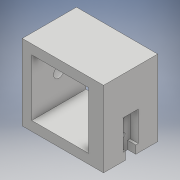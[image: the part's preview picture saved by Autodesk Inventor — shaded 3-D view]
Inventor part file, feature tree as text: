
AUTODESK INVENTOR PART (.ipt)
format: ipt  version: 2017 (Build 210142000, 142)  size: 137,728 bytes
history: native  units: mm
features: extrude x4, sketch x3
ambient origin geometry x8: Origin, YZ Plane, XZ Plane, XY Plane, X Axis, Y Axis, Z Axis, Center Point
bodies: Solid1 (feature_tree)
feature tree (7):
  extrude  "Extrusion1"  Depth=21.0mm
  extrude  "Extrusion2"  Depth=28.0mm
  extrude  "Extrusion3"  Depth=2.5mm
  extrude  "Extrusion4"  Depth=2.5mm
  sketch  "Sketch1"  dims[d0=21.0mm d1=21.0mm]
  sketch  "Sketch4"  dims[d2=28.0mm d3=28.0mm]
  sketch  "Sketch5"  dims[d4=20.0mm d5=0.0mm d6=2.0mm d7=2.8mm d8=2.8mm d10=3.0mm d12=3.0mm d13=0.0mm d14=1.9mm d15=1.9mm d16=6.0mm d17=3.0mm d18=0.0mm d19=3.9mm d20=4.0mm d21=0.0mm d22=2.5mm d24=1.9mm d25=1.9mm]
